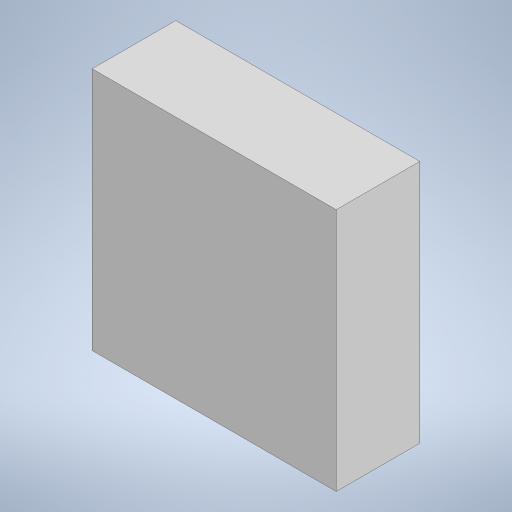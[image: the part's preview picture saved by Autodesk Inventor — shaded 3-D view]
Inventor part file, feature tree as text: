
AUTODESK INVENTOR PART (.ipt)
format: ipt  version: 2023.2 (Build 272271000, 271)  size: 177,664 bytes
history: native  units: mm
features: extrude x1, sketch x1
ambient origin geometry x8: Origin, YZ Plane, XZ Plane, XY Plane, X Axis, Y Axis, Z Axis, Center Point
bodies: Solid1 (feature_tree)
feature tree (2):
  extrude  "Extrusion1"  Depth=14.6mm
  sketch  "Sketch1"  dims[d1=14.6mm d2=14.6mm d3=5.0mm d4=0.0mm]
